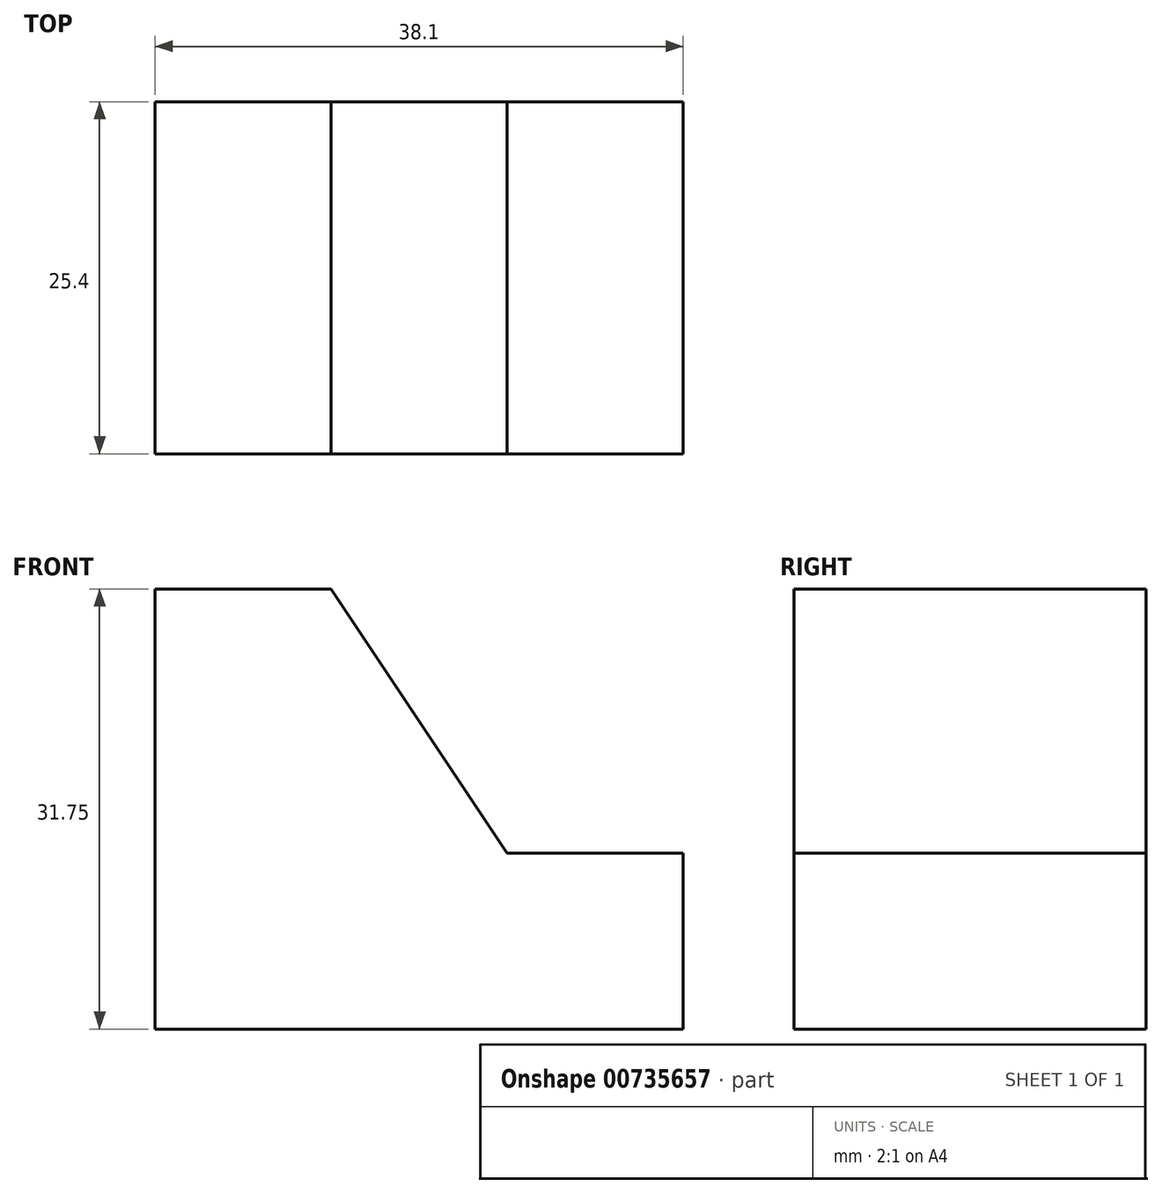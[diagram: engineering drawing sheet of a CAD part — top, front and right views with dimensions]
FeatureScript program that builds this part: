
annotation { "Feature Type Name" : "Feature", "Feature Type Description" : "" }
export const myFeature = defineFeature(function(context is Context, id is Id, definition is map)
    precondition{}
    {
        {
            var Q0;
            Q0=qCreatedBy(makeId("Front.planeOp"),FACE);
            var sketch = newSketch(context, id + "F0", { "sketchPlane" : qUnion([Q0])});
            skLineSegment(sketch, "E0", {"start": v(0, 0) * mm, "end": v(38.1, 0) * mm});
            skLineSegment(sketch, "E1", {"start": v(38.1, 0) * mm, "end": v(38.1, 31.75) * mm});
            skLineSegment(sketch, "E2", {"start": v(38.1, 31.75) * mm, "end": v(0, 31.75) * mm});
            skLineSegment(sketch, "E3", {"start": v(0, 31.75) * mm, "end": v(0, 0) * mm});
            skSolve(sketch);
        }
        {
            var Q0;
            Q0=makeQuery(id+"F0.imprint","IMPRINT",FACE,{"disambiguationData":[TD([[makeQuery(id+"F0.imprint","IMPRINT",EDGE,{"derivedFrom":sQuery(id+"F0.wireOp",EDGE,"E0")}),1.0]])]});
            extrude(context, id + "F1", {"entities" : qUnion([Q0]), "depth" : 25.4 * mm, "offsetDistance" : 25.4 * mm});
        }
        {
            var Q0;
            Q0=makeQuery(id+"F1.opExtrude","CAP_FACE",FACE,{"disambiguationData":[OSD([sQuery(id+"F0.wireOp",EDGE,"E0"),sQuery(id+"F0.wireOp",EDGE,"E1"),sQuery(id+"F0.wireOp",EDGE,"E2"),sQuery(id+"F0.wireOp",EDGE,"E3")])],"isStart":false});
            var sketch = newSketch(context, id + "F2", { "sketchPlane" : qUnion([Q0])});
            skLineSegment(sketch, "E4", {"start": v(12.7, 31.75) * mm, "end": v(25.4, 12.7) * mm});
            skLineSegment(sketch, "E5", {"start": v(25.4, 12.7) * mm, "end": v(38.1, 12.7) * mm});
            skLineSegment(sketch, "E6", {"start": v(25.4, 12.7) * mm, "end": v(25.4, 31.75) * mm});
            skLineSegment(sketch, "E7", {"start": v(25.4, 31.75) * mm, "end": v(12.7, 31.75) * mm});
            skLineSegment(sketch, "E8", {"start": v(25.4, 31.75) * mm, "end": v(38.1, 31.75) * mm});
            skLineSegment(sketch, "E9", {"start": v(38.1, 31.75) * mm, "end": v(38.1, 12.7) * mm});
            skSolve(sketch);
        }
        {
            var Q0;
            Q0=makeQuery(id+"F2.imprint","IMPRINT",FACE,{"disambiguationData":[TD([[makeQuery(id+"F2.imprint","IMPRINT",EDGE,{"derivedFrom":sQuery(id+"F2.wireOp",EDGE,"E4")}),1.0]])]});
            var Q1;
            Q1=makeQuery(id+"F2.imprint","IMPRINT",FACE,{"disambiguationData":[TD([[makeQuery(id+"F2.imprint","IMPRINT",EDGE,{"derivedFrom":sQuery(id+"F2.wireOp",EDGE,"E5")}),1.0]])]});
            extrude(context, id + "F3", {"entities" : qUnion([Q0, Q1]), "operationType" : NewBodyOperationType.REMOVE, "oppositeDirection" : true, "depth" : 25.4 * mm, "offsetDistance" : 25.4 * mm});
        }
    });
